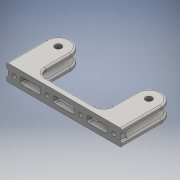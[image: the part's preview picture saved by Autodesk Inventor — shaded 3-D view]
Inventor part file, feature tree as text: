
AUTODESK INVENTOR PART (.ipt)
format: ipt  version: 2016 SP1 (Build 200210100, 210)  size: 326,656 bytes
history: native  units: mm
features: fillet x4, extrude x2, sketch x2, pattern_linear x1
ambient origin geometry x8: Origin, YZ Plane, XZ Plane, XY Plane, X Axis, Y Axis, Z Axis, Center Point
bodies: Solid1 (feature_tree)
feature tree (9):
  extrude  "Extrusion1"  Depth=8.0mm
  fillet  "Fillet1"  Radius=110.0mm
  fillet  "Fillet2"  Radius=55.0mm
  pattern_linear  "Rectangular Pattern2"  Count1=3  [1 undecoded]
  extrude  "Extrusion2"  Depth=15.0mm
  fillet  "Fillet3"  Radius=15.0mm
  fillet  "Fillet4"  Radius=40.0mm
  sketch  "Sketch1"  dims[d0=8.0mm d1=8.0mm d2=110.0mm d3=55.0mm d4=30.0mm]
  sketch  "Sketch2"  dims[d5=30.0mm d6=15.0mm d7=15.0mm d8=40.0mm d9=8.0mm d10=6.0mm d11=0.0mm d12=10.0mm d13=2.0mm d17=20.0mm d19=14.0mm d20=15.0mm d21=15.0mm d22=15.0mm d23=15.0mm d24=25.0mm d25=25.0mm d26=5.0mm d27=5.0mm d28=5.0mm d29=5.0mm d30=7.5mm d31=4.0mm d32=7.5mm d33=4.0mm d34=7.5mm d35=4.0mm d36=4.0mm d37=7.5mm d38=6.0mm d39=0.0mm d40=2.0mm d41=2.0mm]
note: 1 required parameter value undecoded (feature->parameter linkage not recoverable at this tier; creation-order binding heuristic only, values carry confidence <= 0.55)
